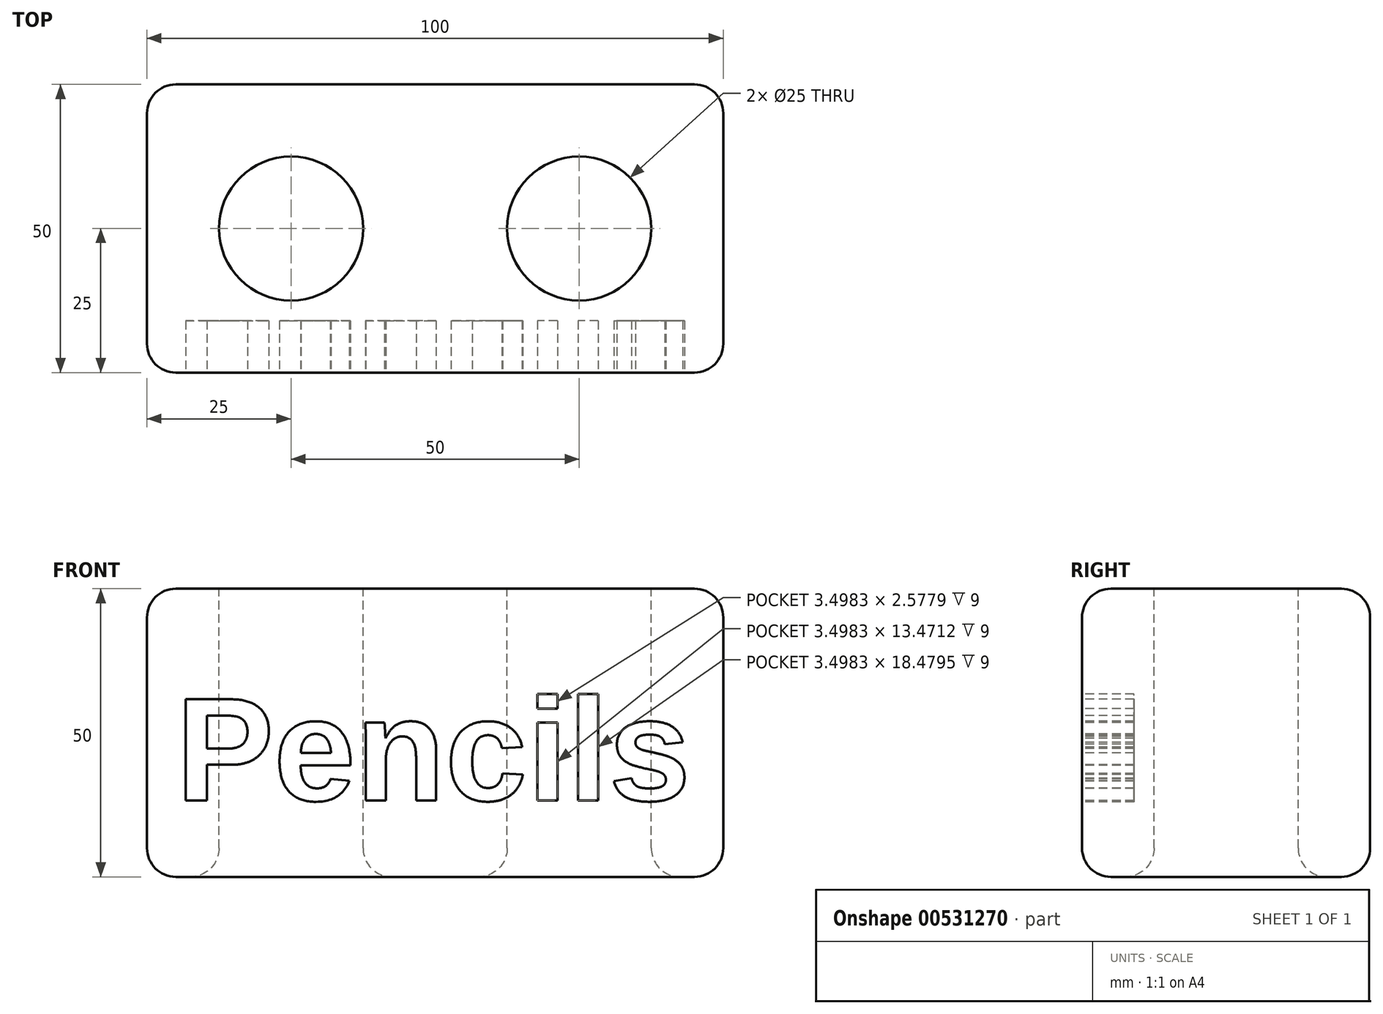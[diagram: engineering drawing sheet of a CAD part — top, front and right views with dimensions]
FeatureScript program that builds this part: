
annotation { "Feature Type Name" : "Feature", "Feature Type Description" : "" }
export const myFeature = defineFeature(function(context is Context, id is Id, definition is map)
    precondition{}
    {
        {
            var Q0;
            Q0=qCreatedBy(makeId("Front.planeOp"),FACE);
            var sketch = newSketch(context, id + "F0", { "sketchPlane" : qUnion([Q0])});
            skLineSegment(sketch, "E0.bottom", {"start": v(-50, 27.27) * mm, "end": v(50, 27.27) * mm});
            skLineSegment(sketch, "E0.top", {"start": v(-50, -22.73) * mm, "end": v(50, -22.73) * mm});
            skLineSegment(sketch, "E0.left", {"start": v(-50, 27.27) * mm, "end": v(-50, -22.73) * mm});
            skLineSegment(sketch, "E0.right", {"start": v(50, 27.27) * mm, "end": v(50, -22.73) * mm});
            skPoint(sketch, "E0.middle", {"position": v(0, 2.27) * mm});
            skSolve(sketch);
        }
        {
            var Q0;
            Q0=makeQuery(id+"F0.imprint","IMPRINT",FACE,{"disambiguationData":[TD([[makeQuery(id+"F0.imprint","IMPRINT",EDGE,{"derivedFrom":sQuery(id+"F0.wireOp",EDGE,"E0.bottom")}),-1.0]])]});
            extrude(context, id + "F1", {"entities" : qUnion([Q0]), "depth" : 50 * mm, "offsetDistance" : 25 * mm});
        }
        {
            var Q0;
            Q0=makeQuery(id+"F1.opExtrude","SWEPT_FACE",FACE,{"disambiguationData":[OSD([sQuery(id+"F0.wireOp",EDGE,"E0.bottom")])]});
            var sketch = newSketch(context, id + "F2", { "sketchPlane" : qUnion([Q0])});
            skLineSegment(sketch, "E1.0", {"start": v(-25, -50) * mm, "end": v(-25, 0) * mm});
            skLineSegment(sketch, "E2.0", {"start": v(45, -5) * mm, "end": v(-45, -5) * mm});
            skLineSegment(sketch, "E2.1", {"start": v(45, -45) * mm, "end": v(45, -5) * mm});
            skLineSegment(sketch, "E2.2", {"start": v(-45, -45) * mm, "end": v(45, -45) * mm});
            skLineSegment(sketch, "E2.3", {"start": v(-45, -5) * mm, "end": v(-45, -45) * mm});
            skLineSegment(sketch, "E3.0", {"start": v(25, -50) * mm, "end": v(25, 0) * mm});
            skCircle(sketch, "E4", {"center": v(-25, -25) * mm, "radius": 12.5 * mm});
            skCircle(sketch, "E5", {"center": v(25, -25) * mm, "radius": 12.5 * mm});
            skSolve(sketch);
        }
        {
            var Q0;
            {var subQ0=sQuery(id+"F2.wireOp",EDGE,"E4");var subQ1=sQuery(id+"F2.wireOp",EDGE,"E1.0");var subQ2=makeQuery(id+"F2.imprint","INTERSECT",VERTEX,{"disambiguationData":[OD(0.0)],"derivedFrom":[subQ1,subQ0]});Q0=makeQuery(id+"F2.imprint","IMPRINT",FACE,{"disambiguationData":[TD([[makeQuery(id+"F2.imprint","IMPRINT",EDGE,{"disambiguationData":[TD([[subQ2,-1.0]])],"derivedFrom":subQ1}),1.0]])]});}
            var Q1;
            {var subQ0=sQuery(id+"F2.wireOp",EDGE,"E4");var subQ1=sQuery(id+"F2.wireOp",EDGE,"E1.0");var subQ2=makeQuery(id+"F2.imprint","INTERSECT",VERTEX,{"disambiguationData":[OD(0.0)],"derivedFrom":[subQ1,subQ0]});Q1=makeQuery(id+"F2.imprint","IMPRINT",FACE,{"disambiguationData":[TD([[makeQuery(id+"F2.imprint","IMPRINT",EDGE,{"disambiguationData":[TD([[subQ2,-1.0]])],"derivedFrom":subQ1}),-1.0]])]});}
            var Q2;
            {var subQ0=sQuery(id+"F2.wireOp",EDGE,"E5");var subQ1=sQuery(id+"F2.wireOp",EDGE,"E3.0");var subQ2=makeQuery(id+"F2.imprint","INTERSECT",VERTEX,{"disambiguationData":[OD(0.0)],"derivedFrom":[subQ1,subQ0]});Q2=makeQuery(id+"F2.imprint","IMPRINT",FACE,{"disambiguationData":[TD([[makeQuery(id+"F2.imprint","IMPRINT",EDGE,{"disambiguationData":[TD([[subQ2,-1.0]])],"derivedFrom":subQ1}),1.0]])]});}
            var Q3;
            {var subQ0=sQuery(id+"F2.wireOp",EDGE,"E5");var subQ1=sQuery(id+"F2.wireOp",EDGE,"E3.0");var subQ2=makeQuery(id+"F2.imprint","INTERSECT",VERTEX,{"disambiguationData":[OD(0.0)],"derivedFrom":[subQ1,subQ0]});Q3=makeQuery(id+"F2.imprint","IMPRINT",FACE,{"disambiguationData":[TD([[makeQuery(id+"F2.imprint","IMPRINT",EDGE,{"disambiguationData":[TD([[subQ2,-1.0]])],"derivedFrom":subQ1}),-1.0]])]});}
            var Q4;
            Q4=sQuery(id+"F2.wireOp",EDGE,"E4");
            var Q5;
            Q5=sQuery(id+"F2.wireOp",EDGE,"E5");
            extrude(context, id + "F3", {"entities" : qUnion([Q0, Q1, Q2, Q3]), "operationType" : NewBodyOperationType.REMOVE, "surfaceEntities" : qUnion([Q4, Q5]), "oppositeDirection" : true, "depth" : 60 * mm, "offsetDistance" : 25 * mm});
        }
        {
            var Q0;
            Q0=makeQuery(id+"F1.opExtrude","CAP_EDGE",EDGE,{"disambiguationData":[OSD([sQuery(id+"F0.wireOp",EDGE,"E0.bottom")])],"isStart":false});
            var Q1;
            Q1=makeQuery(id+"F1.opExtrude","SWEPT_EDGE",EDGE,{"disambiguationData":[OSD([sQuery(id+"F0.wireOp",EDGE,"E0.bottom"),sQuery(id+"F0.wireOp",EDGE,"E0.left")])]});
            var Q2;
            Q2=makeQuery(id+"F1.opExtrude","SWEPT_EDGE",EDGE,{"disambiguationData":[OSD([sQuery(id+"F0.wireOp",EDGE,"E0.bottom"),sQuery(id+"F0.wireOp",EDGE,"E0.right")])]});
            var Q3;
            Q3=makeQuery(id+"F1.opExtrude","CAP_EDGE",EDGE,{"disambiguationData":[OSD([sQuery(id+"F0.wireOp",EDGE,"E0.bottom")])],"isStart":true});
            var Q4;
            Q4=makeQuery(id+"F3.boolean.opBoolean","COPY",EDGE,{"derivedFrom":makeQuery(id+"F3.opExtrude","CAP_EDGE",EDGE,{"disambiguationData":[OSD([sQuery(id+"F2.wireOp",EDGE,"E5")])],"isStart":true})});
            var Q5;
            Q5=makeQuery(id+"F1.opExtrude","SWEPT_EDGE",EDGE,{"disambiguationData":[OSD([sQuery(id+"F0.wireOp",EDGE,"E0.top"),sQuery(id+"F0.wireOp",EDGE,"E0.left")])]});
            var Q6;
            Q6=makeQuery(id+"F1.opExtrude","SWEPT_EDGE",EDGE,{"disambiguationData":[OSD([sQuery(id+"F0.wireOp",EDGE,"E0.top"),sQuery(id+"F0.wireOp",EDGE,"E0.right")])]});
            var Q7;
            Q7=makeQuery(id+"F3.boolean.opBoolean","COPY",EDGE,{"derivedFrom":makeQuery(id+"F3.opExtrude","CAP_EDGE",EDGE,{"disambiguationData":[OSD([sQuery(id+"F2.wireOp",EDGE,"E4")])],"isStart":true})});
            var Q8;
            Q8=makeQuery(id+"F1.opExtrude","CAP_EDGE",EDGE,{"disambiguationData":[OSD([sQuery(id+"F0.wireOp",EDGE,"E0.top")])],"isStart":true});
            var Q9;
            Q9=makeQuery(id+"F1.opExtrude","CAP_EDGE",EDGE,{"disambiguationData":[OSD([sQuery(id+"F0.wireOp",EDGE,"E0.top")])],"isStart":false});
            var Q10;
            Q10=makeQuery(id+"F1.opExtrude","CAP_EDGE",EDGE,{"disambiguationData":[OSD([sQuery(id+"F0.wireOp",EDGE,"E0.left")])],"isStart":false});
            var Q11;
            Q11=makeQuery(id+"F1.opExtrude","CAP_EDGE",EDGE,{"disambiguationData":[OSD([sQuery(id+"F0.wireOp",EDGE,"E0.right")])],"isStart":false});
            var Q12;
            Q12=makeQuery(id+"F3.boolean.opBoolean","INTERSECT",EDGE,{"derivedFrom":[makeQuery(id+"F1.opExtrude","SWEPT_FACE",FACE,{"disambiguationData":[OSD([sQuery(id+"F0.wireOp",EDGE,"E0.top")])]}),makeQuery(id+"F3.opExtrude","SWEPT_FACE",FACE,{"disambiguationData":[OSD([sQuery(id+"F2.wireOp",EDGE,"E4")])]})]});
            var Q13;
            Q13=makeQuery(id+"F3.boolean.opBoolean","INTERSECT",EDGE,{"derivedFrom":[makeQuery(id+"F1.opExtrude","SWEPT_FACE",FACE,{"disambiguationData":[OSD([sQuery(id+"F0.wireOp",EDGE,"E0.top")])]}),makeQuery(id+"F3.opExtrude","SWEPT_FACE",FACE,{"disambiguationData":[OSD([sQuery(id+"F2.wireOp",EDGE,"E5")])]})]});
            var Q14;
            Q14=makeQuery(id+"F1.opExtrude","CAP_EDGE",EDGE,{"disambiguationData":[OSD([sQuery(id+"F0.wireOp",EDGE,"E0.left")])],"isStart":true});
            var Q15;
            Q15=makeQuery(id+"F1.opExtrude","CAP_EDGE",EDGE,{"disambiguationData":[OSD([sQuery(id+"F0.wireOp",EDGE,"E0.right")])],"isStart":true});
            fillet(context, id + "F4", {"entities" : qUnion([Q0, Q1, Q2, Q3, Q4, Q5, Q6, Q7, Q8, Q9, Q10, Q11, Q12, Q13, Q14, Q15]), "radius" : 5 * mm, "tangentPropagation" : true, "allowEdgeOverflow" : false});
        }
        {
            var Q0;
            Q0=makeQuery(id+"F1.opExtrude","CAP_FACE",FACE,{"disambiguationData":[OSD([sQuery(id+"F0.wireOp",EDGE,"E0.bottom"),sQuery(id+"F0.wireOp",EDGE,"E0.top"),sQuery(id+"F0.wireOp",EDGE,"E0.left"),sQuery(id+"F0.wireOp",EDGE,"E0.right")])],"isStart":false});
            var sketch = newSketch(context, id + "F5", { "sketchPlane" : qUnion([Q0])});
            skText(sketch, "E6", { "text": "Pencils", "fontName": "Arimo-Bold.ttf"});
            const initialGuessF5  = {"E6": [-0.045, -0.00946, 1, 0, 0.01836]};
            skSetInitialGuess(sketch, initialGuessF5);
            skSolve(sketch);
        }
        {
            var Q0;
            Q0 = qSketchRegion(id + "F5", true);
            extrude(context, id + "F6", {"entities" : qUnion([Q0]), "operationType" : NewBodyOperationType.REMOVE, "oppositeDirection" : true, "depth" : 9 * mm, "offsetDistance" : 25 * mm});
        }
    });
